# Revit family: Furniture-Table-Casual-Naughtone-Trace_Circular_Table_Large
name_source: partatom
category: Furniture
revit_build: Autodesk Revit 2014 (Build: 20130308_1515(x64)
units: mm (PartAtom-declared; Revit-internal decimal feet)

## types (2) — shared parameters
COBie Description = Designed by InTheDetail, The trace table range is simply a modern classic that speaks for itself. Suffice to say, the immaculate hand made steel frame and repetition of shapes make trace an exquisitely balanced form.
Current Revision = 1
Height = 750 mm  [stored 2.46063 ft]
Manufacturer = Naughtone
Name = Furniture-Table-Casual-Naughtone-Trace
Product URL = http://www.naughtone.com
Type Comments = Trace Table Large
URL = http://www.naughtone.com
Uniclass = Pr_40_50_21_58
WarrantyDuration = 60
zero-valued in all types: Barcode, Cost, SerialNumber, TagNumber

## per-type parameters (varying)
| type | Depth | Description | Length | Model | TypeName |
| TRA-1200 | 1200 mm  [stored 3.93701 ft] | Trace Circular Table 1200mm | 1200 mm  [stored 3.93701 ft] | Trace Circular Table 1200mm | 1200mmx1200mmx750mm, Trace Table Large |
| TRA-1400 | 1400 mm  [stored 4.59318 ft] | Trace Circular Table 1400mm | 1400 mm  [stored 4.59318 ft] | Trace Circular Table 1400mm | 1400mmx1400mmx750mm, Trace Table Large |

note: column(s) folded — value = type name in every type: AssetIdentifier, Product Code

note: [stored X ft] marks values corroborated as IEEE doubles in the binary element streams (Revit-internal decimal feet)

## geometry (parser evidence)
native form markers: Sweep x1
no freeform markers — native parametric forms only
